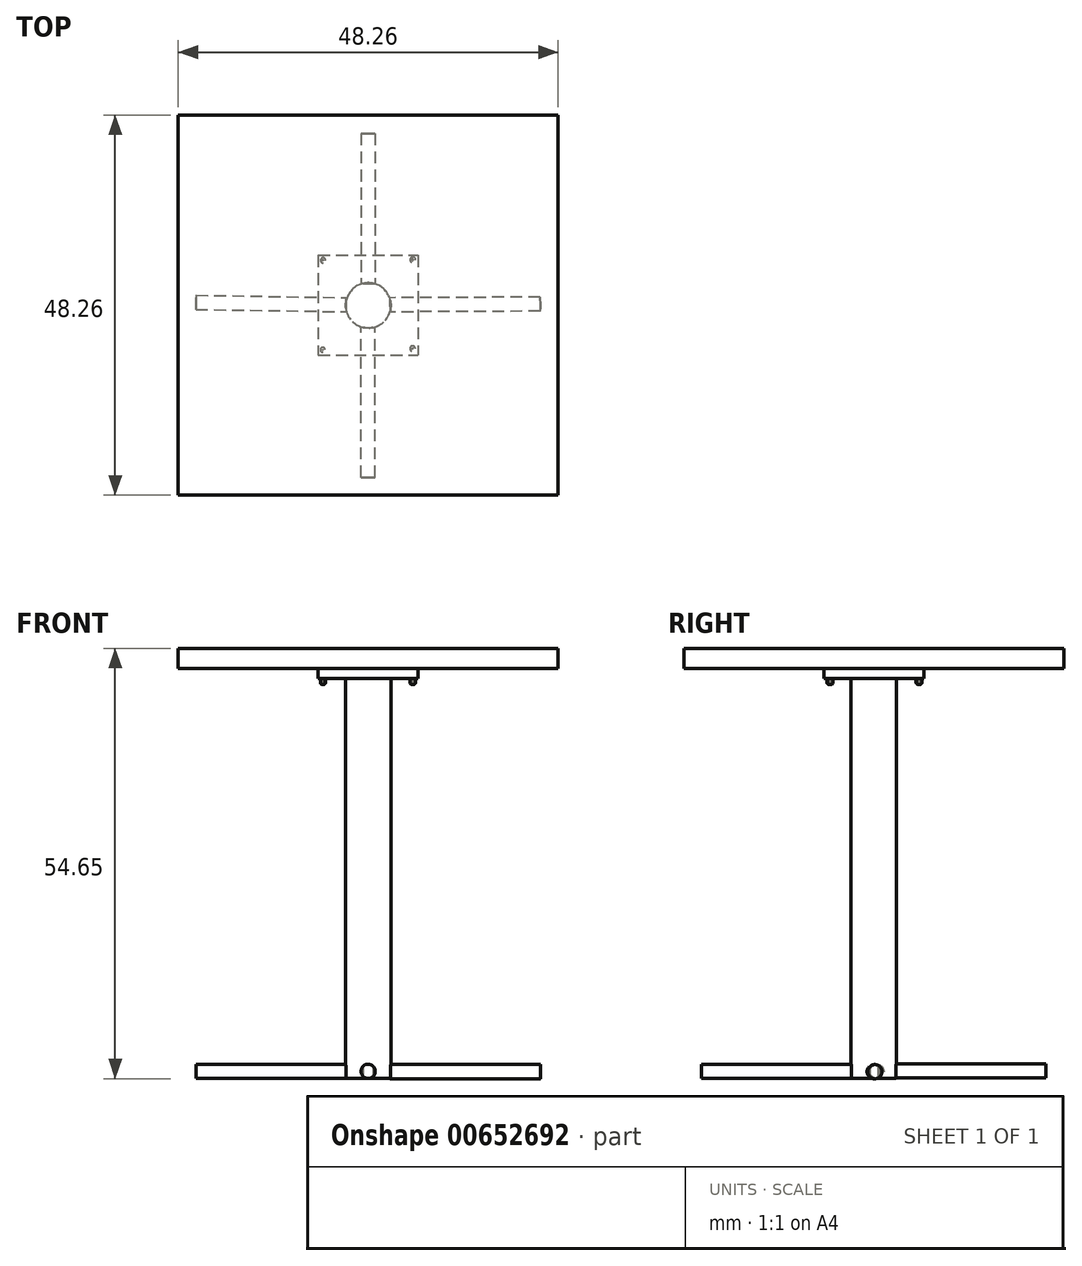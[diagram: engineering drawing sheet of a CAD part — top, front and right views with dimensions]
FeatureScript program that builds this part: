
annotation { "Feature Type Name" : "Feature", "Feature Type Description" : "" }
export const myFeature = defineFeature(function(context is Context, id is Id, definition is map)
    precondition{}
    {
        {
            var Q0;
            Q0=qCreatedBy(makeId("Top.planeOp"),FACE);
            var sketch = newSketch(context, id + "F0", { "sketchPlane" : qUnion([Q0])});
            skLineSegment(sketch, "E0.bottom", {"start": v(24.13, 24.13) * mm, "end": v(-24.13, 24.13) * mm});
            skLineSegment(sketch, "E0.top", {"start": v(24.13, -24.13) * mm, "end": v(-24.13, -24.13) * mm});
            skLineSegment(sketch, "E0.left", {"start": v(24.13, 24.13) * mm, "end": v(24.13, -24.13) * mm});
            skLineSegment(sketch, "E0.right", {"start": v(-24.13, 24.13) * mm, "end": v(-24.13, -24.13) * mm});
            skPoint(sketch, "E0.middle", {"position": v(0, 0) * mm});
            skSolve(sketch);
        }
        {
            var Q0;
            Q0 = qSketchRegion(id + "F0", true);
            extrude(context, id + "F1", {"entities" : qUnion([Q0]), "depth" : 2.54 * mm, "offsetDistance" : 25.4 * mm});
        }
        {
            var Q0;
            Q0=makeQuery(id+"F1.opExtrude","CAP_FACE",FACE,{"disambiguationData":[OSD([sQuery(id+"F0.wireOp",EDGE,"E0.bottom"),sQuery(id+"F0.wireOp",EDGE,"E0.top"),sQuery(id+"F0.wireOp",EDGE,"E0.left"),sQuery(id+"F0.wireOp",EDGE,"E0.right")])],"isStart":true});
            var sketch = newSketch(context, id + "F2", { "sketchPlane" : qUnion([Q0])});
            skLineSegment(sketch, "E1.bottom", {"start": v(-6.35, -6.35) * mm, "end": v(6.35, -6.35) * mm});
            skLineSegment(sketch, "E1.top", {"start": v(-6.35, 6.35) * mm, "end": v(6.35, 6.35) * mm});
            skLineSegment(sketch, "E1.left", {"start": v(-6.35, -6.35) * mm, "end": v(-6.35, 6.35) * mm});
            skLineSegment(sketch, "E1.right", {"start": v(6.35, -6.35) * mm, "end": v(6.35, 6.35) * mm});
            skPoint(sketch, "E1.middle", {"position": v(0, 0) * mm});
            skSolve(sketch);
        }
        {
            var Q0;
            Q0 = qSketchRegion(id + "F2", true);
            extrude(context, id + "F3", {"entities" : qUnion([Q0]), "operationType" : NewBodyOperationType.ADD, "depth" : 1.27 * mm, "offsetDistance" : 25.4 * mm});
        }
        {
            var Q0;
            Q0=makeQuery(id+"F3.opExtrude","CAP_FACE",FACE,{"disambiguationData":[OSD([sQuery(id+"F2.wireOp",EDGE,"E1.bottom"),sQuery(id+"F2.wireOp",EDGE,"E1.top"),sQuery(id+"F2.wireOp",EDGE,"E1.left"),sQuery(id+"F2.wireOp",EDGE,"E1.right")])],"isStart":false});
            var sketch = newSketch(context, id + "F4", { "sketchPlane" : qUnion([Q0])});
            skCircle(sketch, "E2", {"center": v(0.01, 0.04) * mm, "radius": 2.87 * mm});
            skPoint(sketch, "E2.first.point", {"position": v(2.88, 0) * mm});
            skPoint(sketch, "E2.second.point", {"position": v(-2.86, 0) * mm});
            skPoint(sketch, "E2.third.point", {"position": v(0, 2.92) * mm});
            skSolve(sketch);
        }
        {
            var Q0;
            Q0 = qSketchRegion(id + "F4", true);
            extrude(context, id + "F5", {"entities" : qUnion([Q0]), "operationType" : NewBodyOperationType.ADD, "depth" : 50.8 * mm, "offsetDistance" : 25.4 * mm});
        }
        {
            var Q0;
            Q0=makeQuery(id+"F3.opExtrude","CAP_FACE",FACE,{"disambiguationData":[OSD([sQuery(id+"F2.wireOp",EDGE,"E1.bottom"),sQuery(id+"F2.wireOp",EDGE,"E1.top"),sQuery(id+"F2.wireOp",EDGE,"E1.left"),sQuery(id+"F2.wireOp",EDGE,"E1.right")])],"isStart":false});
            var sketch = newSketch(context, id + "F6", { "sketchPlane" : qUnion([Q0])});
            skCircle(sketch, "E3", {"center": v(-5.77, 5.69) * mm, "radius": 0.3 * mm});
            skCircle(sketch, "E4", {"center": v(-5.72, -5.67) * mm, "radius": 0.33 * mm});
            skCircle(sketch, "E5", {"center": v(5.67, -5.74) * mm, "radius": 0.36 * mm});
            skCircle(sketch, "E6", {"center": v(5.65, 5.55) * mm, "radius": 0.35 * mm});
            skSolve(sketch);
        }
        {
            var Q0;
            Q0 = qSketchRegion(id + "F6", true);
            extrude(context, id + "F7", {"entities" : qUnion([Q0]), "operationType" : NewBodyOperationType.ADD, "depth" : 0.76 * mm, "offsetDistance" : 25.4 * mm});
        }
        {
            var Q0;
            Q0=makeQuery(id+"F7.opExtrude","CAP_EDGE",EDGE,{"disambiguationData":[OSD([sQuery(id+"F6.wireOp",EDGE,"E3")])],"isStart":false});
            var Q1;
            Q1=makeQuery(id+"F7.opExtrude","CAP_FACE",FACE,{"disambiguationData":[OSD([sQuery(id+"F6.wireOp",EDGE,"E5")])],"isStart":false});
            var Q2;
            Q2=makeQuery(id+"F7.opExtrude","CAP_EDGE",EDGE,{"disambiguationData":[OSD([sQuery(id+"F6.wireOp",EDGE,"E4")])],"isStart":false});
            var Q3;
            Q3=makeQuery(id+"F7.opExtrude","CAP_EDGE",EDGE,{"disambiguationData":[OSD([sQuery(id+"F6.wireOp",EDGE,"E6")])],"isStart":false});
            fillet(context, id + "F8", {"entities" : qUnion([Q0, Q1, Q2, Q3]), "radius" : 0.25 * mm, "tangentPropagation" : true, "allowEdgeOverflow" : false});
        }
        {
            var Q0;
            Q0=makeQuery(id+"F7.opExtrude","CAP_FACE",FACE,{"disambiguationData":[OSD([sQuery(id+"F6.wireOp",EDGE,"E5")])],"isStart":false});
            var sketch = newSketch(context, id + "F9", { "sketchPlane" : qUnion([Q0])});
            skLineSegment(sketch, "E7.bottom", {"start": v(5.78, -5.75) * mm, "end": v(5.57, -5.75) * mm});
            skLineSegment(sketch, "E7.top", {"start": v(5.78, -5.73) * mm, "end": v(5.57, -5.73) * mm});
            skLineSegment(sketch, "E7.left", {"start": v(5.78, -5.75) * mm, "end": v(5.78, -5.73) * mm});
            skLineSegment(sketch, "E7.right", {"start": v(5.57, -5.75) * mm, "end": v(5.57, -5.73) * mm});
            skPoint(sketch, "E7.middle", {"position": v(5.67, -5.74) * mm});
            skLineSegment(sketch, "E8.bottom", {"start": v(5.66, -5.64) * mm, "end": v(5.68, -5.64) * mm});
            skLineSegment(sketch, "E8.top", {"start": v(5.66, -5.84) * mm, "end": v(5.68, -5.84) * mm});
            skLineSegment(sketch, "E8.left", {"start": v(5.66, -5.64) * mm, "end": v(5.66, -5.84) * mm});
            skLineSegment(sketch, "E8.right", {"start": v(5.68, -5.64) * mm, "end": v(5.68, -5.84) * mm});
            skSolve(sketch);
        }
        {
            var Q0;
            Q0=makeQuery(id+"F7.opExtrude","CAP_FACE",FACE,{"disambiguationData":[OSD([sQuery(id+"F6.wireOp",EDGE,"E6")])],"isStart":false});
            var sketch = newSketch(context, id + "F10", { "sketchPlane" : qUnion([Q0])});
            skLineSegment(sketch, "E9.bottom", {"start": v(5.74, 5.54) * mm, "end": v(5.55, 5.54) * mm});
            skLineSegment(sketch, "E9.top", {"start": v(5.74, 5.55) * mm, "end": v(5.55, 5.55) * mm});
            skLineSegment(sketch, "E9.left", {"start": v(5.74, 5.54) * mm, "end": v(5.74, 5.55) * mm});
            skLineSegment(sketch, "E9.right", {"start": v(5.55, 5.54) * mm, "end": v(5.55, 5.55) * mm});
            skPoint(sketch, "E9.middle", {"position": v(5.65, 5.55) * mm});
            skLineSegment(sketch, "E10.bottom", {"start": v(5.64, 5.64) * mm, "end": v(5.65, 5.64) * mm});
            skLineSegment(sketch, "E10.top", {"start": v(5.64, 5.45) * mm, "end": v(5.65, 5.45) * mm});
            skLineSegment(sketch, "E10.left", {"start": v(5.64, 5.64) * mm, "end": v(5.64, 5.45) * mm});
            skLineSegment(sketch, "E10.right", {"start": v(5.65, 5.64) * mm, "end": v(5.65, 5.45) * mm});
            skSolve(sketch);
        }
        {
            var Q0;
            Q0=makeQuery(id+"F7.opExtrude","CAP_FACE",FACE,{"disambiguationData":[OSD([sQuery(id+"F6.wireOp",EDGE,"E3")])],"isStart":false});
            var sketch = newSketch(context, id + "F11", { "sketchPlane" : qUnion([Q0])});
            skLineSegment(sketch, "E11.bottom", {"start": v(-5.83, 5.68) * mm, "end": v(-5.72, 5.68) * mm});
            skLineSegment(sketch, "E11.top", {"start": v(-5.83, 5.7) * mm, "end": v(-5.72, 5.7) * mm});
            skLineSegment(sketch, "E11.left", {"start": v(-5.83, 5.68) * mm, "end": v(-5.83, 5.7) * mm});
            skLineSegment(sketch, "E11.right", {"start": v(-5.72, 5.68) * mm, "end": v(-5.72, 5.7) * mm});
            skPoint(sketch, "E11.middle", {"position": v(-5.77, 5.69) * mm});
            skLineSegment(sketch, "E12.bottom", {"start": v(-5.78, 5.74) * mm, "end": v(-5.76, 5.74) * mm});
            skLineSegment(sketch, "E12.top", {"start": v(-5.78, 5.63) * mm, "end": v(-5.76, 5.63) * mm});
            skLineSegment(sketch, "E12.left", {"start": v(-5.78, 5.74) * mm, "end": v(-5.78, 5.63) * mm});
            skLineSegment(sketch, "E12.right", {"start": v(-5.76, 5.74) * mm, "end": v(-5.76, 5.63) * mm});
            skSolve(sketch);
        }
        {
            var Q0;
            Q0=makeQuery(id+"F7.opExtrude","CAP_FACE",FACE,{"disambiguationData":[OSD([sQuery(id+"F6.wireOp",EDGE,"E4")])],"isStart":false});
            var sketch = newSketch(context, id + "F12", { "sketchPlane" : qUnion([Q0])});
            skLineSegment(sketch, "E13.bottom", {"start": v(-5.65, -5.68) * mm, "end": v(-5.8, -5.68) * mm});
            skLineSegment(sketch, "E13.top", {"start": v(-5.65, -5.66) * mm, "end": v(-5.8, -5.66) * mm});
            skLineSegment(sketch, "E13.left", {"start": v(-5.65, -5.68) * mm, "end": v(-5.65, -5.66) * mm});
            skLineSegment(sketch, "E13.right", {"start": v(-5.8, -5.68) * mm, "end": v(-5.8, -5.66) * mm});
            skPoint(sketch, "E13.middle", {"position": v(-5.72, -5.67) * mm});
            skLineSegment(sketch, "E14.bottom", {"start": v(-5.73, -5.6) * mm, "end": v(-5.7, -5.6) * mm});
            skLineSegment(sketch, "E14.top", {"start": v(-5.73, -5.74) * mm, "end": v(-5.7, -5.74) * mm});
            skLineSegment(sketch, "E14.left", {"start": v(-5.73, -5.6) * mm, "end": v(-5.73, -5.74) * mm});
            skLineSegment(sketch, "E14.right", {"start": v(-5.7, -5.6) * mm, "end": v(-5.7, -5.74) * mm});
            skSolve(sketch);
        }
        {
            var Q0;
            Q0 = qSketchRegion(id + "F12", true);
            var Q1;
            {var subQ0=sQuery(id+"F11.wireOp",EDGE,"E11.left");Q1=makeQuery(id+"F11.imprint","IMPRINT",FACE,{"disambiguationData":[TD([[makeQuery(id+"F11.imprint","IMPRINT",EDGE,{"derivedFrom":subQ0}),-1.0]])]});}
            var Q2;
            {var subQ0=sQuery(id+"F11.wireOp",EDGE,"E11.right");Q2=makeQuery(id+"F11.imprint","IMPRINT",FACE,{"disambiguationData":[TD([[makeQuery(id+"F11.imprint","IMPRINT",EDGE,{"derivedFrom":subQ0}),1.0]])]});}
            var Q3;
            {var subQ0=sQuery(id+"F11.wireOp",EDGE,"E12.left");var subQ1=sQuery(id+"F11.wireOp",EDGE,"E11.bottom");var subQ2=makeQuery(id+"F11.imprint","INTERSECT",VERTEX,{"derivedFrom":[subQ1,subQ0]});Q3=makeQuery(id+"F11.imprint","IMPRINT",FACE,{"disambiguationData":[TD([[makeQuery(id+"F11.imprint","IMPRINT",EDGE,{"disambiguationData":[TD([[subQ2,-1.0]])],"derivedFrom":subQ1}),1.0]])]});}
            var Q4;
            {var subQ5=sQuery(id+"F11.wireOp",EDGE,"E12.top");Q4=makeQuery(id+"F11.imprint","IMPRINT",FACE,{"disambiguationData":[TD([[makeQuery(id+"F11.imprint","IMPRINT",EDGE,{"derivedFrom":subQ5}),1.0]])]});}
            var Q5;
            {var subQ5=sQuery(id+"F11.wireOp",EDGE,"E12.bottom");Q5=makeQuery(id+"F11.imprint","IMPRINT",FACE,{"disambiguationData":[TD([[makeQuery(id+"F11.imprint","IMPRINT",EDGE,{"derivedFrom":subQ5}),-1.0]])]});}
            var Q6;
            Q6 = qSketchRegion(id + "F10", true);
            var Q7;
            Q7 = qSketchRegion(id + "F9", true);
            extrude(context, id + "F13", {"entities" : qUnion([Q0, Q1, Q2, Q3, Q4, Q5, Q6, Q7]), "operationType" : NewBodyOperationType.REMOVE, "oppositeDirection" : true, "depth" : 0.5 * mm, "offsetDistance" : 25.4 * mm});
        }
        {
            var Q0;
            Q0=makeQuery(id+"F5.opExtrude","CAP_FACE",FACE,{"disambiguationData":[OSD([sQuery(id+"F4.wireOp",EDGE,"E2")])],"isStart":false});
            var sketch = newSketch(context, id + "F14", { "sketchPlane" : qUnion([Q0])});
            skLineSegment(sketch, "E15", {"start": v(-0.62, 2.84) * mm, "end": v(0.65, 2.84) * mm});
            skLineSegment(sketch, "E16", {"start": v(-0.62, 2.84) * mm, "end": v(0, 3.2) * mm});
            skLineSegment(sketch, "E17", {"start": v(0, 3.2) * mm, "end": v(0.65, 2.84) * mm});
            skSolve(sketch);
        }
        {
            var Q0;
            Q0 = qSketchRegion(id + "F14", true);
            extrude(context, id + "F15", {"entities" : qUnion([Q0]), "operationType" : NewBodyOperationType.REMOVE, "oppositeDirection" : true, "depth" : 1.41 * mm, "offsetDistance" : 25.4 * mm});
        }
        {
            var Q0;
            Q0=makeQuery(id+"F15.boolean.opBoolean","COPY",FACE,{"derivedFrom":makeQuery(id+"F15.opExtrude","SWEPT_FACE",FACE,{"disambiguationData":[OSD([sQuery(id+"F14.wireOp",EDGE,"E15")])]})});
            var sketch = newSketch(context, id + "F16", { "sketchPlane" : qUnion([Q0])});
            skCircle(sketch, "E18", {"center": v(0, -51.17) * mm, "radius": 0.9 * mm});
            skSolve(sketch);
        }
        {
            var Q0;
            Q0 = qSketchRegion(id + "F16", true);
            extrude(context, id + "F17", {"entities" : qUnion([Q0]), "operationType" : NewBodyOperationType.ADD, "depth" : 19.05 * mm, "offsetDistance" : 25.4 * mm});
        }
        {
            var Q0;
            Q0=makeQuery(id+"F5.opExtrude","CAP_FACE",FACE,{"disambiguationData":[OSD([sQuery(id+"F4.wireOp",EDGE,"E2")])],"isStart":false});
            var sketch = newSketch(context, id + "F18", { "sketchPlane" : qUnion([Q0])});
            skLineSegment(sketch, "E19", {"start": v(2.81, 0.66) * mm, "end": v(2.8, -0.6) * mm});
            skLineSegment(sketch, "E20", {"start": v(2.81, 0.66) * mm, "end": v(3.06, 0) * mm});
            skLineSegment(sketch, "E21", {"start": v(3.06, 0) * mm, "end": v(2.8, -0.6) * mm});
            skSolve(sketch);
        }
        {
            var Q0;
            Q0 = qSketchRegion(id + "F18", true);
            extrude(context, id + "F19", {"entities" : qUnion([Q0]), "operationType" : NewBodyOperationType.REMOVE, "oppositeDirection" : true, "depth" : 1.02 * mm, "offsetDistance" : 25.4 * mm});
        }
        {
            var Q0;
            Q0=makeQuery(id+"F19.boolean.opBoolean","COPY",FACE,{"derivedFrom":makeQuery(id+"F19.opExtrude","SWEPT_FACE",FACE,{"disambiguationData":[OSD([sQuery(id+"F18.wireOp",EDGE,"E19")])]})});
            var sketch = newSketch(context, id + "F20", { "sketchPlane" : qUnion([Q0])});
            skCircle(sketch, "E22", {"center": v(0, -51.22) * mm, "radius": 0.9 * mm});
            skSolve(sketch);
        }
        {
            var Q0;
            Q0 = qSketchRegion(id + "F20", true);
            extrude(context, id + "F21", {"entities" : qUnion([Q0]), "operationType" : NewBodyOperationType.ADD, "depth" : 19.05 * mm, "offsetDistance" : 25.4 * mm});
        }
        {
            var Q0;
            Q0=makeQuery(id+"F5.opExtrude","CAP_FACE",FACE,{"disambiguationData":[OSD([sQuery(id+"F4.wireOp",EDGE,"E2")])],"isStart":false});
            var sketch = newSketch(context, id + "F22", { "sketchPlane" : qUnion([Q0])});
            skLineSegment(sketch, "E23", {"start": v(-0.66, -2.75) * mm, "end": v(0.68, -2.75) * mm});
            skLineSegment(sketch, "E24", {"start": v(-0.66, -2.75) * mm, "end": v(0, -2.97) * mm});
            skLineSegment(sketch, "E25", {"start": v(0, -2.97) * mm, "end": v(0.68, -2.75) * mm});
            skSolve(sketch);
        }
        {
            var Q0;
            Q0 = qSketchRegion(id + "F22", true);
            extrude(context, id + "F23", {"entities" : qUnion([Q0]), "operationType" : NewBodyOperationType.REMOVE, "oppositeDirection" : true, "depth" : 1.27 * mm, "offsetDistance" : 25.4 * mm});
        }
        {
            var Q0;
            Q0=makeQuery(id+"F23.boolean.opBoolean","COPY",FACE,{"derivedFrom":makeQuery(id+"F23.opExtrude","SWEPT_FACE",FACE,{"disambiguationData":[OSD([sQuery(id+"F22.wireOp",EDGE,"E23")])]})});
            var sketch = newSketch(context, id + "F24", { "sketchPlane" : qUnion([Q0])});
            skCircle(sketch, "E26", {"center": v(0, -51.13) * mm, "radius": 0.9 * mm});
            skSolve(sketch);
        }
        {
            var Q0;
            Q0 = qSketchRegion(id + "F24", true);
            extrude(context, id + "F25", {"entities" : qUnion([Q0]), "operationType" : NewBodyOperationType.ADD, "depth" : 19.05 * mm, "offsetDistance" : 25.4 * mm});
        }
        {
            var Q0;
            Q0=makeQuery(id+"F5.opExtrude","CAP_FACE",FACE,{"disambiguationData":[OSD([sQuery(id+"F4.wireOp",EDGE,"E2")])],"isStart":false});
            var sketch = newSketch(context, id + "F26", { "sketchPlane" : qUnion([Q0])});
            skLineSegment(sketch, "E27", {"start": v(-2.82, 0) * mm, "end": v(-2.8, -0.5) * mm});
            skLineSegment(sketch, "E28", {"start": v(-2.8, -0.5) * mm, "end": v(-2.82, 0.5) * mm});
            skLineSegment(sketch, "E29", {"start": v(-2.82, 0.5) * mm, "end": v(-3, 0) * mm});
            skLineSegment(sketch, "E30", {"start": v(-3, 0) * mm, "end": v(-2.8, -0.5) * mm});
            skSolve(sketch);
        }
        {
            var Q0;
            Q0 = qSketchRegion(id + "F26", true);
            extrude(context, id + "F27", {"entities" : qUnion([Q0]), "operationType" : NewBodyOperationType.REMOVE, "oppositeDirection" : true, "depth" : 1.2 * mm, "offsetDistance" : 25.4 * mm});
        }
        {
            var Q0;
            Q0=makeQuery(id+"F27.boolean.opBoolean","COPY",FACE,{"derivedFrom":makeQuery(id+"F27.opExtrude","SWEPT_FACE",FACE,{"disambiguationData":[OSD([sQuery(id+"F26.wireOp",EDGE,"E28")])]})});
            var sketch = newSketch(context, id + "F28", { "sketchPlane" : qUnion([Q0])});
            skCircle(sketch, "E31", {"center": v(0, -51.19) * mm, "radius": 0.9 * mm});
            skSolve(sketch);
        }
        {
            var Q0;
            Q0 = qSketchRegion(id + "F28", true);
            extrude(context, id + "F29", {"entities" : qUnion([Q0]), "operationType" : NewBodyOperationType.ADD, "depth" : 19.05 * mm, "offsetDistance" : 25.4 * mm});
        }
    });
